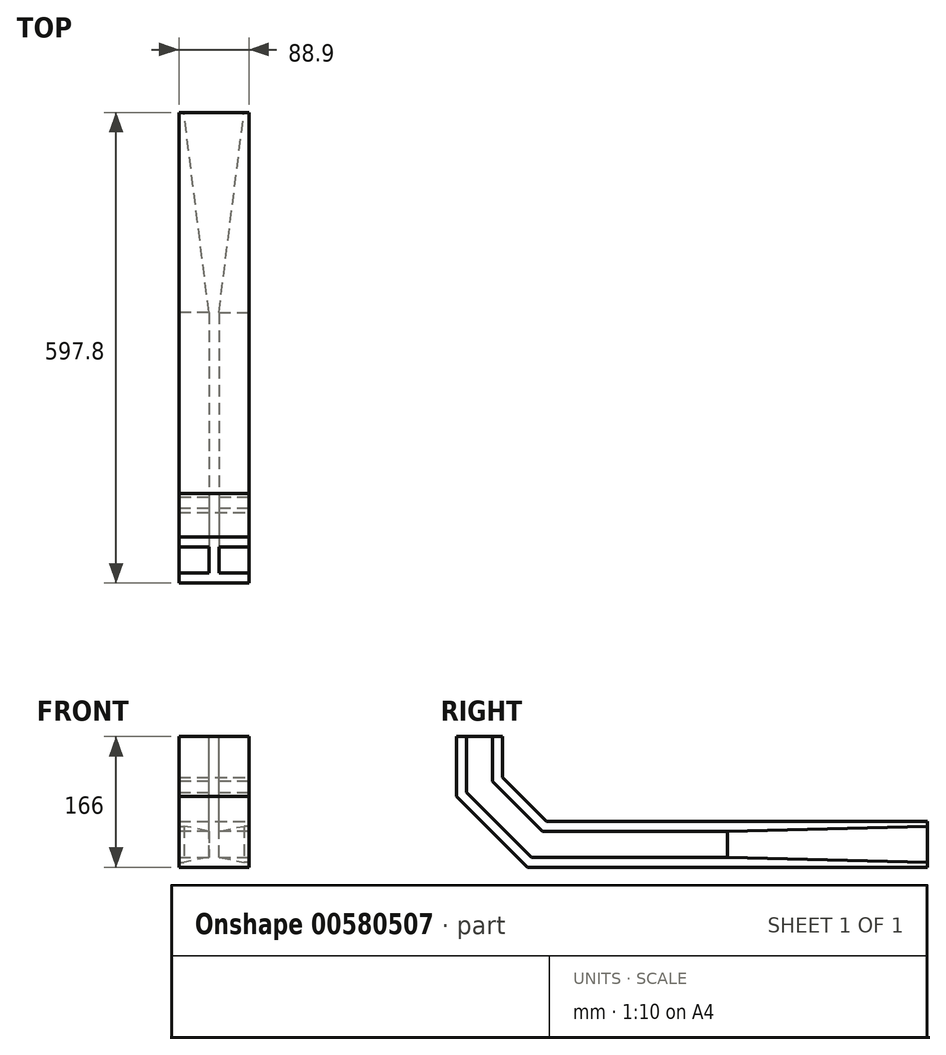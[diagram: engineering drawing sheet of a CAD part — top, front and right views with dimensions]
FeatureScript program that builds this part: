
annotation { "Feature Type Name" : "Feature", "Feature Type Description" : "" }
export const myFeature = defineFeature(function(context is Context, id is Id, definition is map)
    precondition{}
    {
        {
            var Q0;
            Q0=qCreatedBy(makeId("Front.planeOp"),FACE);
            var sketch = newSketch(context, id + "F0", { "sketchPlane" : qUnion([Q0])});
            skLineSegment(sketch, "E0", {"start": v(-88.9, 0) * mm, "end": v(0, 0) * mm});
            skLineSegment(sketch, "E1", {"start": v(0, 0) * mm, "end": v(0, 12.7) * mm});
            skLineSegment(sketch, "E2", {"start": v(0, 12.7) * mm, "end": v(-38.1, 12.7) * mm});
            skLineSegment(sketch, "E3", {"start": v(-38.1, 12.7) * mm, "end": v(-38.1, 45.72) * mm});
            skLineSegment(sketch, "E4", {"start": v(-38.1, 45.72) * mm, "end": v(0, 45.72) * mm});
            skLineSegment(sketch, "E5", {"start": v(0, 45.72) * mm, "end": v(0, 58.42) * mm});
            skLineSegment(sketch, "E6", {"start": v(0, 58.42) * mm, "end": v(-88.9, 58.42) * mm});
            skLineSegment(sketch, "E7", {"start": v(-88.9, 58.42) * mm, "end": v(-88.9, 45.72) * mm});
            skLineSegment(sketch, "E8", {"start": v(-88.9, 45.72) * mm, "end": v(-50.8, 45.72) * mm});
            skLineSegment(sketch, "E9", {"start": v(-50.8, 45.72) * mm, "end": v(-50.8, 12.7) * mm});
            skLineSegment(sketch, "E10", {"start": v(-50.8, 12.7) * mm, "end": v(-88.9, 12.7) * mm});
            skLineSegment(sketch, "E11", {"start": v(-88.9, 12.7) * mm, "end": v(-88.9, 0) * mm});
            skSolve(sketch);
        }
        {
            var Q0;
            Q0=qCreatedBy(makeId("Right.planeOp"),FACE);
            var sketch = newSketch(context, id + "F1", { "sketchPlane" : qUnion([Q0])});
            skLineSegment(sketch, "E12", {"start": v(0, 0) * mm, "end": v(-254, 0) * mm});
            skLineSegment(sketch, "E13", {"start": v(-254, 0) * mm, "end": v(-343.8, 89.8) * mm});
            skLineSegment(sketch, "E14", {"start": v(-343.8, 89.8) * mm, "end": v(-343.8, 166) * mm});
            skSolve(sketch);
        }
        {
            var Q0;
            Q0=makeQuery(id+"F0.imprint","IMPRINT",FACE,{"disambiguationData":[TD([[makeQuery(id+"F0.imprint","IMPRINT",EDGE,{"derivedFrom":sQuery(id+"F0.wireOp",EDGE,"E0")}),1.0]])]});
            var Q1;
            Q1=sQuery(id+"F1.wireOp",EDGE,"E12");
            var Q2;
            Q2=sQuery(id+"F1.wireOp",EDGE,"E13");
            var Q3;
            Q3=sQuery(id+"F1.wireOp",EDGE,"E14");
            sweep(context, id + "F2", {"profiles" : qUnion([Q0]), "path" : qUnion([Q1, Q2, Q3])});
        }
        {
            var Q0;
            Q0=qCreatedBy(makeId("Front.planeOp"),FACE);
            cPlane(context, id + "F3", {"entities" : qUnion([Q0]), "cplaneType" : CPlaneType.OFFSET, "offset" : 254 * mm, "oppositeDirection" : true, "width" : 152.4 * mm, "height" : 152.4 * mm});
        }
        {
            var Q0;
            Q0=qCreatedBy(id+"F3.planeOp",FACE);
            var sketch = newSketch(context, id + "F4", { "sketchPlane" : qUnion([Q0])});
            skLineSegment(sketch, "E15.bottom", {"start": v(0, 0) * mm, "end": v(-88.9, 0) * mm});
            skLineSegment(sketch, "E15.top", {"start": v(0, 58.42) * mm, "end": v(-88.9, 58.42) * mm});
            skLineSegment(sketch, "E15.left", {"start": v(0, 0) * mm, "end": v(0, 58.42) * mm});
            skLineSegment(sketch, "E15.right", {"start": v(-88.9, 0) * mm, "end": v(-88.9, 58.42) * mm});
            skPoint(sketch, "E16.0", {"position": v(-88.9, 58.42) * mm});
            skLineSegment(sketch, "E17.bottom", {"start": v(-88.9, 52.07) * mm, "end": v(-82.55, 52.07) * mm});
            skLineSegment(sketch, "E17.top", {"start": v(-88.9, 6.35) * mm, "end": v(-82.55, 6.35) * mm});
            skLineSegment(sketch, "E17.left", {"start": v(-88.9, 52.07) * mm, "end": v(-88.9, 6.35) * mm});
            skLineSegment(sketch, "E17.right", {"start": v(-82.55, 52.07) * mm, "end": v(-82.55, 6.35) * mm});
            skLineSegment(sketch, "E18.bottom", {"start": v(0, 52.07) * mm, "end": v(-6.35, 52.07) * mm});
            skLineSegment(sketch, "E18.top", {"start": v(0, 6.35) * mm, "end": v(-6.35, 6.35) * mm});
            skLineSegment(sketch, "E18.left", {"start": v(0, 52.07) * mm, "end": v(0, 6.35) * mm});
            skLineSegment(sketch, "E18.right", {"start": v(-6.35, 52.07) * mm, "end": v(-6.35, 6.35) * mm});
            skSolve(sketch);
        }
        {
            var Q1;
            Q1=makeQuery(id+"F2.opSweep","CAP_FACE",FACE,{"disambiguationData":[OSD([sQuery(id+"F0.wireOp",EDGE,"E0"),sQuery(id+"F0.wireOp",EDGE,"E1"),sQuery(id+"F0.wireOp",EDGE,"E2"),sQuery(id+"F0.wireOp",EDGE,"E3"),sQuery(id+"F0.wireOp",EDGE,"E4"),sQuery(id+"F0.wireOp",EDGE,"E5"),sQuery(id+"F0.wireOp",EDGE,"E6"),sQuery(id+"F0.wireOp",EDGE,"E7"),sQuery(id+"F0.wireOp",EDGE,"E8"),sQuery(id+"F0.wireOp",EDGE,"E9"),sQuery(id+"F0.wireOp",EDGE,"E10"),sQuery(id+"F0.wireOp",EDGE,"E11"),sQuery(id+"F1.wireOp",VERTEX,"E12.start")])],"isStart":true});
            var Q2;
            {var subQ6=sQuery(id+"F4.wireOp",EDGE,"E15.bottom");Q2=makeQuery(id+"F4.imprint","IMPRINT",FACE,{"disambiguationData":[TD([[makeQuery(id+"F4.imprint","IMPRINT",EDGE,{"derivedFrom":subQ6}),-1.0]])]});}
            loft(context, id + "F5", {"operationType" : NewBodyOperationType.ADD, "sheetProfilesArray" : [{ "sheetProfileEntities" : qUnion([Q1]) }, { "sheetProfileEntities" : qUnion([Q2]) }]});
        }
    });
